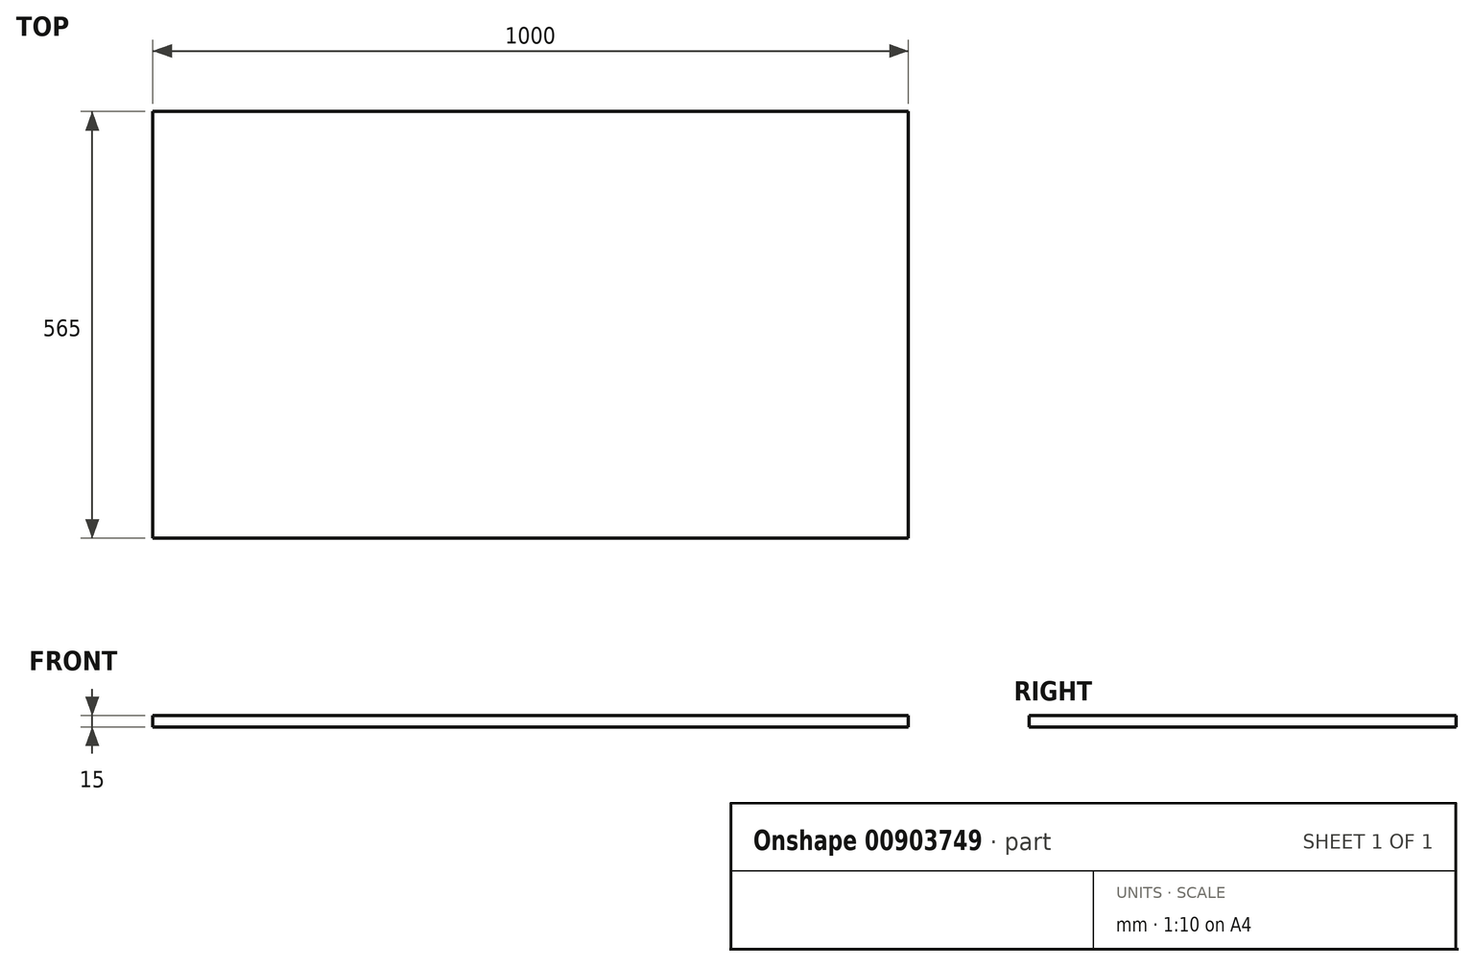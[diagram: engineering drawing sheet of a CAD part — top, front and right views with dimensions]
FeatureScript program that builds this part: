
annotation { "Feature Type Name" : "Feature", "Feature Type Description" : "" }
export const myFeature = defineFeature(function(context is Context, id is Id, definition is map)
    precondition{}
    {
        {
            var Q0;
            Q0=qCreatedBy(makeId("Top.planeOp"),FACE);
            var sketch = newSketch(context, id + "F0", { "sketchPlane" : qUnion([Q0])});
            skLineSegment(sketch, "E0.bottom", {"start": v(-500, 282.5) * mm, "end": v(500, 282.5) * mm});
            skLineSegment(sketch, "E0.top", {"start": v(-500, -282.5) * mm, "end": v(500, -282.5) * mm});
            skLineSegment(sketch, "E0.left", {"start": v(-500, 282.5) * mm, "end": v(-500, -282.5) * mm});
            skLineSegment(sketch, "E0.right", {"start": v(500, 282.5) * mm, "end": v(500, -282.5) * mm});
            skSolve(sketch);
        }
        {
            var Q0;
            Q0=makeQuery(id+"F0.imprint","IMPRINT",FACE,{"disambiguationData":[TD([[makeQuery(id+"F0.imprint","IMPRINT",EDGE,{"derivedFrom":sQuery(id+"F0.wireOp",EDGE,"E0.bottom")}),-1.0]])]});
            extrude(context, id + "F1", {"entities" : qUnion([Q0]), "depth" : 15 * mm, "offsetDistance" : 25 * mm});
        }
    });
